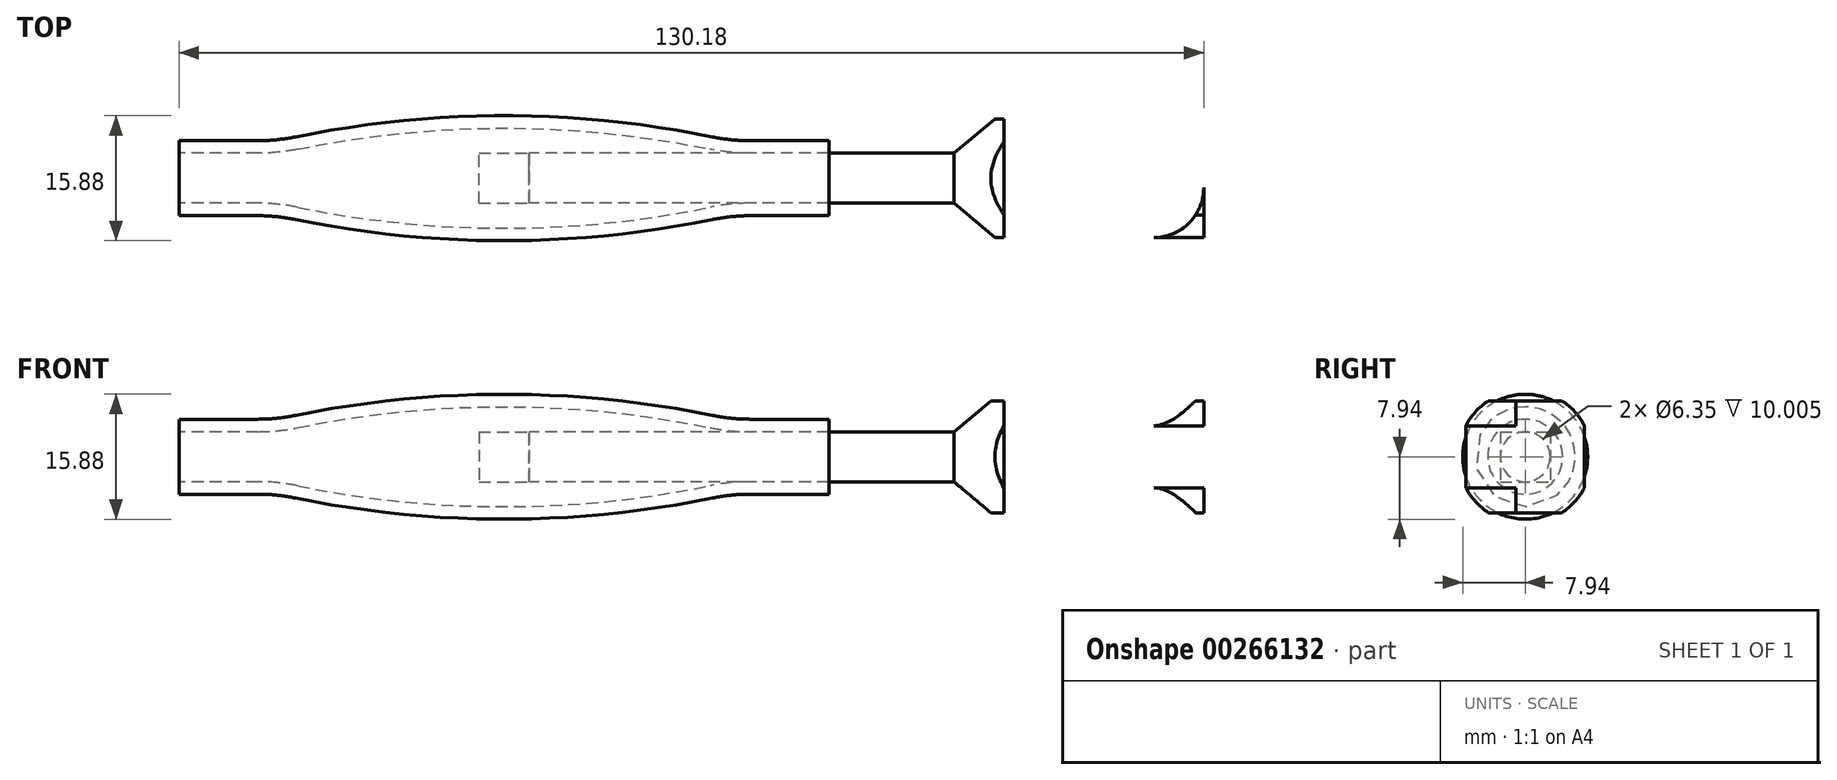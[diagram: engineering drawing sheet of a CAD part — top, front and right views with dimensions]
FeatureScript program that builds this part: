
annotation { "Feature Type Name" : "Feature", "Feature Type Description" : "" }
export const myFeature = defineFeature(function(context is Context, id is Id, definition is map)
    precondition{}
    {
        {
            var Q0;
            Q0=qCreatedBy(makeId("Top.planeOp"),FACE);
            var sketch = newSketch(context, id + "F0", { "sketchPlane" : qUnion([Q0])});
            skLineSegment(sketch, "E0", {"start": v(-41.28, 0) * mm, "end": v(-41.28, 3.18) * mm, "construction": true});
            skLineSegment(sketch, "E1", {"start": v(-24.47, 0) * mm, "end": v(27.99, 0) * mm, "construction": true});
            skLineSegment(sketch, "E2", {"start": v(0, -19.61) * mm, "end": v(0, 27.4) * mm, "construction": true});
            skLineSegment(sketch, "E3.MirrorCS", {"start": v(41.28, 0) * mm, "end": v(41.28, 3.18) * mm, "construction": true});
            skLineSegment(sketch, "E4", {"start": v(-41.28, 3.18) * mm, "end": v(-31.27, 3.18) * mm});
            skLineSegment(sketch, "E5.MirrorCS", {"start": v(41.28, 3.18) * mm, "end": v(31.27, 3.18) * mm});
            skArc(sketch, "E6", {"start": v(26.16, 3.7) * mm, "mid": v(0, 6.35) * mm, "end": v(-26.16, 3.7) * mm});
            skPoint(sketch, "E7.visualSharp", {"position": v(-28.58, 3.18) * mm});
            skArc(sketch, "E7.filletArc", {"start": v(-31.27, 3.18) * mm, "mid": v(-28.7, 3.3) * mm, "end": v(-26.16, 3.7) * mm});
            skPoint(sketch, "E8.visualSharp", {"position": v(28.58, 3.18) * mm});
            skArc(sketch, "E8.filletArc", {"start": v(26.16, 3.7) * mm, "mid": v(28.7, 3.3) * mm, "end": v(31.27, 3.17) * mm});
            skLineSegment(sketch, "E9.0", {"start": v(41.28, 4.76) * mm, "end": v(31.27, 4.76) * mm});
            skArc(sketch, "E10.0", {"start": v(26.48, 5.25) * mm, "mid": v(28.86, 4.88) * mm, "end": v(31.27, 4.76) * mm});
            skArc(sketch, "E11.0", {"start": v(26.48, 5.25) * mm, "mid": v(0, 7.94) * mm, "end": v(-26.48, 5.25) * mm});
            skArc(sketch, "E12.0", {"start": v(-31.27, 4.76) * mm, "mid": v(-28.86, 4.88) * mm, "end": v(-26.48, 5.25) * mm});
            skLineSegment(sketch, "E13.0", {"start": v(-41.28, 4.76) * mm, "end": v(-31.27, 4.76) * mm});
            skLineSegment(sketch, "E14", {"start": v(-41.28, 4.76) * mm, "end": v(-41.28, 3.18) * mm});
            skLineSegment(sketch, "E15", {"start": v(41.28, 4.76) * mm, "end": v(41.28, 3.18) * mm});
            skSolve(sketch);
        }
        {
            var Q0;
            Q0=makeQuery(id+"F0.imprint","IMPRINT",FACE,{"disambiguationData":[TD([[makeQuery(id+"F0.imprint","IMPRINT",EDGE,{"derivedFrom":sQuery(id+"F0.wireOp",EDGE,"E4")}),1.0]])]});
            var Q1;
            Q1=sQuery(id+"F0.wireOp",EDGE,"E1");
            revolve(context, id + "F7", {"entities" : qUnion([Q0]), "axis" : qUnion([Q1]), "revolveType" : RevolveType.FULL});
        }
        {
            var Q0;
            Q0=qCreatedBy(makeId("Top.planeOp"),FACE);
            var sketch = newSketch(context, id + "F1", { "sketchPlane" : qUnion([Q0])});
            skLineSegment(sketch, "E16.bottom", {"start": v(-3.17, -3.17) * mm, "end": v(3.18, -3.17) * mm});
            skLineSegment(sketch, "E16.top", {"start": v(-3.18, 3.18) * mm, "end": v(3.17, 3.18) * mm});
            skLineSegment(sketch, "E16.left", {"start": v(-3.17, -3.17) * mm, "end": v(-3.18, 3.18) * mm});
            skLineSegment(sketch, "E16.right", {"start": v(3.18, -3.17) * mm, "end": v(3.17, 3.18) * mm});
            skSolve(sketch);
        }
        {
            var Q0;
            Q0=makeQuery(id+"F1.imprint","IMPRINT",FACE,{"disambiguationData":[TD([[makeQuery(id+"F1.imprint","IMPRINT",EDGE,{"derivedFrom":sQuery(id+"F1.wireOp",EDGE,"E16.bottom")}),1.0]])]});
            extrude(context, id + "F2", {"entities" : qUnion([Q0]), "endBound" : BoundingType.SYMMETRIC, "depth" : 6.35 * mm});
        }
        {
            var Q0;
            Q0=makeQuery(id+"F2.opExtrude","SWEPT_FACE",FACE,{"disambiguationData":[OSD([sQuery(id+"F1.wireOp",EDGE,"E16.right")])]});
            var sketch = newSketch(context, id + "F8", { "sketchPlane" : qUnion([Q0])});
            skCircle(sketch, "E17", {"center": v(0, 0) * mm, "radius": 3.18 * mm});
            skSolve(sketch);
        }
        {
            var Q0;
            {var subQ0=sQuery(id+"F8.wireOp",EDGE,"E17");var subQ1=sQuery(id+"F1.wireOp",EDGE,"E16.right");var subQ2=makeQuery(id+"F8.imprint","INTERSECT",VERTEX,{"derivedFrom":[makeQuery(id+"F2.opExtrude","CAP_EDGE",EDGE,{"disambiguationData":[OSD([subQ1])],"isStart":false}),subQ0]});Q0=makeQuery(id+"F8.imprint","IMPRINT",FACE,{"disambiguationData":[TD([[makeQuery(id+"F8.imprint","IMPRINT",EDGE,{"disambiguationData":[TD([[subQ2,1.0]])],"derivedFrom":subQ0}),1.0]])]});}
            extrude(context, id + "F3", {"entities" : qUnion([Q0]), "depth" : 53.97 * mm});
        }
        {
            var Q0;
            Q0=qCreatedBy(makeId("Top.planeOp"),FACE);
            var sketch = newSketch(context, id + "F9", { "sketchPlane" : qUnion([Q0])});
            skLineSegment(sketch, "E18", {"start": v(57.15, 0) * mm, "end": v(57.15, 3.18) * mm});
            skLineSegment(sketch, "E19", {"start": v(57.15, 3.18) * mm, "end": v(63.5, 8.5) * mm});
            skLineSegment(sketch, "E20", {"start": v(63.5, 8.5) * mm, "end": v(63.5, 0) * mm, "construction": true});
            skLineSegment(sketch, "E21", {"start": v(63.5, 0) * mm, "end": v(57.15, 0) * mm});
            skLineSegment(sketch, "E22", {"start": v(63.5, 8.5) * mm, "end": v(88.9, 8.5) * mm});
            skLineSegment(sketch, "E23", {"start": v(88.9, 8.5) * mm, "end": v(88.9, 0) * mm});
            skLineSegment(sketch, "E24", {"start": v(88.9, 0) * mm, "end": v(63.5, 0) * mm});
            skSolve(sketch);
        }
        {
            var Q0;
            Q0=makeQuery(id+"F9.imprint","IMPRINT",FACE,{"disambiguationData":[TD([[makeQuery(id+"F9.imprint","IMPRINT",EDGE,{"derivedFrom":sQuery(id+"F9.wireOp",EDGE,"E18")}),-1.0]])]});
            var Q1;
            Q1=sQuery(id+"F0.wireOp",EDGE,"E1");
            revolve(context, id + "F4", {"operationType" : NewBodyOperationType.ADD, "entities" : qUnion([Q0]), "axis" : qUnion([Q1]), "revolveType" : RevolveType.FULL});
        }
        {
            var Q0;
            Q0=qCreatedBy(makeId("Top.planeOp"),FACE);
            var sketch = newSketch(context, id + "F5", { "sketchPlane" : qUnion([Q0])});
            skCircle(sketch, "E25", {"center": v(76.2, 0) * mm, "radius": 3.17 * mm});
            skSolve(sketch);
        }
        {
            var Q0;
            Q0=makeQuery(id+"F5.imprint","IMPRINT",FACE,{"disambiguationData":[TD([[makeQuery(id+"F5.imprint","IMPRINT",EDGE,{"derivedFrom":sQuery(id+"F5.wireOp",EDGE,"E25")}),1.0]])]});
            extrude(context, id + "F10", {"entities" : qUnion([Q0]), "operationType" : NewBodyOperationType.REMOVE, "endBound" : BoundingType.SYMMETRIC, "oppositeDirection" : true, "depth" : 25.4 * mm});
        }
        {
            var Q0;
            Q0=qCreatedBy(makeId("Front.planeOp"),FACE);
            var sketch = newSketch(context, id + "F6", { "sketchPlane" : qUnion([Q0])});
            skLineSegment(sketch, "E26", {"start": v(90.17, 7.11) * mm, "end": v(58.42, 7.11) * mm});
            skLineSegment(sketch, "E27", {"start": v(58.42, 7.11) * mm, "end": v(58.42, 12.2) * mm});
            skLineSegment(sketch, "E28", {"start": v(58.42, 12.2) * mm, "end": v(90.17, 12.2) * mm});
            skLineSegment(sketch, "E29", {"start": v(90.17, 12.2) * mm, "end": v(90.17, 7.11) * mm});
            skLineSegment(sketch, "E30", {"start": v(90.17, 3.94) * mm, "end": v(90.17, -3.94) * mm});
            skLineSegment(sketch, "E31", {"start": v(90.17, -3.94) * mm, "end": v(63.5, -3.94) * mm});
            skLineSegment(sketch, "E32", {"start": v(63.5, -3.94) * mm, "end": v(63.5, 3.94) * mm});
            skLineSegment(sketch, "E33", {"start": v(63.5, 3.94) * mm, "end": v(90.17, 3.94) * mm});
            skLineSegment(sketch, "E34.MirrorCS", {"start": v(90.17, -7.11) * mm, "end": v(58.42, -7.11) * mm});
            skLineSegment(sketch, "E35.MirrorCS", {"start": v(58.42, -7.11) * mm, "end": v(58.42, -12.2) * mm});
            skLineSegment(sketch, "E36.MirrorCS", {"start": v(58.42, -12.2) * mm, "end": v(90.17, -12.2) * mm});
            skLineSegment(sketch, "E37.MirrorCS", {"start": v(90.17, -12.2) * mm, "end": v(90.17, -7.11) * mm});
            skSolve(sketch);
        }
        {
            var Q0;
            Q0=makeQuery(id+"F6.imprint","IMPRINT",FACE,{"disambiguationData":[TD([[makeQuery(id+"F6.imprint","IMPRINT",EDGE,{"derivedFrom":sQuery(id+"F6.wireOp",EDGE,"E30")}),-1.0]])]});
            var Q1;
            Q1=makeQuery(id+"F6.imprint","IMPRINT",FACE,{"disambiguationData":[TD([[makeQuery(id+"F6.imprint","IMPRINT",EDGE,{"derivedFrom":sQuery(id+"F6.wireOp",EDGE,"E34.MirrorCS")}),1.0]])]});
            var Q2;
            Q2=makeQuery(id+"F6.imprint","IMPRINT",FACE,{"disambiguationData":[TD([[makeQuery(id+"F6.imprint","IMPRINT",EDGE,{"derivedFrom":sQuery(id+"F6.wireOp",EDGE,"E26")}),-1.0]])]});
            extrude(context, id + "F11", {"entities" : qUnion([Q0, Q1, Q2]), "operationType" : NewBodyOperationType.REMOVE, "endBound" : BoundingType.SYMMETRIC, "oppositeDirection" : true, "depth" : 25.4 * mm});
        }
        {
            var Q0;
            Q0=makeQuery(id+"F11.boolean.opBoolean","SPLIT",FACE,{"disambiguationData":[TD([makeQuery(id+"F11.opExtrude","SWEPT_FACE",FACE,{"disambiguationData":[OSD([sQuery(id+"F6.wireOp",EDGE,"E26")])]})])],"derivedFrom":makeQuery(id+"F4.opRevolve","SWEPT_FACE",FACE,{"disambiguationData":[OSD([sQuery(id+"F9.wireOp",EDGE,"E23")])]})});
            var sketch = newSketch(context, id + "F12", { "sketchPlane" : qUnion([Q0])});
            skLineSegment(sketch, "E38", {"start": v(-7.54, 3.94) * mm, "end": v(-7.54, -5.84) * mm});
            skLineSegment(sketch, "E39", {"start": v(-7.54, -5.84) * mm, "end": v(-10.77, -5.84) * mm});
            skLineSegment(sketch, "E40", {"start": v(-10.77, -5.84) * mm, "end": v(-10.77, 3.94) * mm});
            skLineSegment(sketch, "E41", {"start": v(-10.77, 3.94) * mm, "end": v(-7.54, 3.94) * mm});
            skLineSegment(sketch, "E42", {"start": v(0, 17.15) * mm, "end": v(0, -15.62) * mm, "construction": true});
            skLineSegment(sketch, "E43.MirrorCS", {"start": v(7.54, 3.94) * mm, "end": v(7.54, -5.84) * mm});
            skLineSegment(sketch, "E44.MirrorCS", {"start": v(10.77, -5.84) * mm, "end": v(10.77, 3.94) * mm});
            skLineSegment(sketch, "E45.MirrorCS", {"start": v(10.77, 3.94) * mm, "end": v(7.54, 3.94) * mm});
            skLineSegment(sketch, "E46.MirrorCS", {"start": v(7.54, -5.84) * mm, "end": v(10.77, -5.84) * mm});
            skSolve(sketch);
        }
        {
            var Q0;
            Q0=makeQuery(id+"F12.imprint","IMPRINT",FACE,{"disambiguationData":[TD([[makeQuery(id+"F12.imprint","IMPRINT",EDGE,{"derivedFrom":sQuery(id+"F12.wireOp",EDGE,"E38")}),-1.0]])]});
            var Q1;
            Q1=makeQuery(id+"F12.imprint","IMPRINT",FACE,{"disambiguationData":[TD([[makeQuery(id+"F12.imprint","IMPRINT",EDGE,{"derivedFrom":sQuery(id+"F12.wireOp",EDGE,"E43.MirrorCS")}),1.0]])]});
            extrude(context, id + "F13", {"entities" : qUnion([Q0, Q1]), "operationType" : NewBodyOperationType.REMOVE, "oppositeDirection" : true, "depth" : 50.8 * mm});
        }
        {
            var Q0;
            Q0=makeQuery(id+"F11.boolean.opBoolean","COPY",FACE,{"derivedFrom":makeQuery(id+"F11.opExtrude","SWEPT_FACE",FACE,{"disambiguationData":[OSD([sQuery(id+"F6.wireOp",EDGE,"E31")])]})});
            var sketch = newSketch(context, id + "F14", { "sketchPlane" : qUnion([Q0])});
            skLineSegment(sketch, "E47", {"start": v(82.55, 7.54) * mm, "end": v(81.36, 7.54) * mm});
            skLineSegment(sketch, "E48", {"start": v(88.9, 1.19) * mm, "end": v(88.9, 0) * mm});
            skLineSegment(sketch, "E49", {"start": v(104.73, 0) * mm, "end": v(56.18, 0) * mm, "construction": true});
            skPoint(sketch, "E50.visualSharp", {"position": v(88.9, 7.54) * mm});
            skArc(sketch, "E50.filletArc", {"start": v(88.9, 1.19) * mm, "mid": v(87.04, 5.68) * mm, "end": v(82.55, 7.54) * mm});
            skLineSegment(sketch, "E51", {"start": v(82.55, 7.54) * mm, "end": v(88.9, 7.54) * mm});
            skLineSegment(sketch, "E52", {"start": v(88.9, 1.19) * mm, "end": v(88.9, 7.54) * mm});
            skArc(sketch, "E53.MirrorCS", {"start": v(88.9, -1.19) * mm, "mid": v(87.04, -5.68) * mm, "end": v(82.55, -7.54) * mm});
            skLineSegment(sketch, "E54.MirrorCS", {"start": v(82.55, -7.54) * mm, "end": v(88.9, -7.54) * mm});
            skLineSegment(sketch, "E55.MirrorCS", {"start": v(88.9, -1.19) * mm, "end": v(88.9, -7.54) * mm});
            skSolve(sketch);
        }
        {
            var Q0;
            Q0=makeQuery(id+"F14.imprint","IMPRINT",FACE,{"disambiguationData":[TD([[makeQuery(id+"F14.imprint","IMPRINT",EDGE,{"derivedFrom":sQuery(id+"F14.wireOp",EDGE,"E50.filletArc")}),-1.0]])]});
            var Q1;
            Q1=makeQuery(id+"F14.imprint","IMPRINT",FACE,{"disambiguationData":[TD([[makeQuery(id+"F14.imprint","IMPRINT",EDGE,{"derivedFrom":sQuery(id+"F14.wireOp",EDGE,"E53.MirrorCS")}),1.0]])]});
            extrude(context, id + "F15", {"entities" : qUnion([Q0, Q1]), "operationType" : NewBodyOperationType.REMOVE, "endBound" : BoundingType.SYMMETRIC, "oppositeDirection" : true, "depth" : 50.8 * mm});
        }
    });
